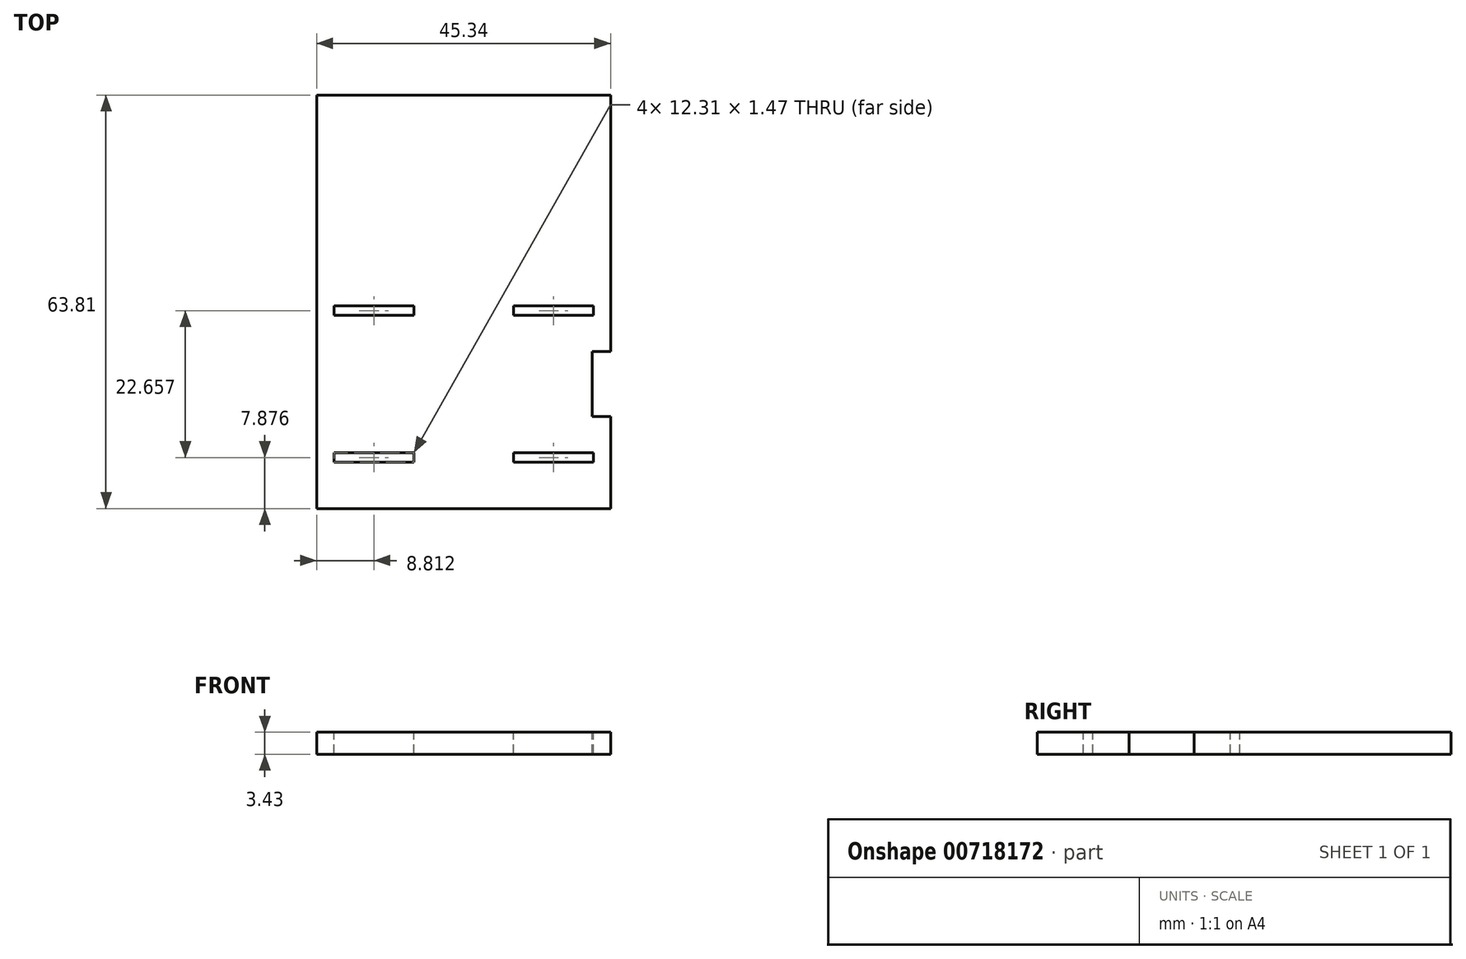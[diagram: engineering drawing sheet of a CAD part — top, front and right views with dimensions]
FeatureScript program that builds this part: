
annotation { "Feature Type Name" : "Feature", "Feature Type Description" : "" }
export const myFeature = defineFeature(function(context is Context, id is Id, definition is map)
    precondition{}
    {
        {
            var Q0;
            Q0=qCreatedBy(makeId("Top.planeOp"),FACE);
            var sketch = newSketch(context, id + "F0", { "sketchPlane" : qUnion([Q0])});
            skLineSegment(sketch, "E0.bottom", {"start": v(-23.55, 31.02) * mm, "end": v(21.8, 31.02) * mm});
            skLineSegment(sketch, "E0.top", {"start": v(-23.55, -7.39) * mm, "end": v(21.8, -7.39) * mm});
            skLineSegment(sketch, "E0.left", {"start": v(-23.55, 31.02) * mm, "end": v(-23.55, -7.39) * mm});
            skLineSegment(sketch, "E0.right", {"start": v(21.8, 31.02) * mm, "end": v(21.8, -7.39) * mm});
            skSolve(sketch);
        }
        {
            var Q0;
            Q0=makeQuery(id+"F0.imprint","IMPRINT",FACE,{"disambiguationData":[TD([[makeQuery(id+"F0.imprint","IMPRINT",EDGE,{"derivedFrom":sQuery(id+"F0.wireOp",EDGE,"E0.bottom")}),-1.0]])]});
            extrude(context, id + "F1", {"entities" : qUnion([Q0]), "depth" : 3.43 * mm, "offsetDistance" : 25.4 * mm});
        }
        {
            var Q0;
            Q0=makeQuery(id+"F1.opExtrude","CAP_FACE",FACE,{"disambiguationData":[OSD([sQuery(id+"F0.wireOp",EDGE,"E0.bottom"),sQuery(id+"F0.wireOp",EDGE,"E0.top"),sQuery(id+"F0.wireOp",EDGE,"E0.left"),sQuery(id+"F0.wireOp",EDGE,"E0.right")])],"isStart":false});
            var sketch = newSketch(context, id + "F2", { "sketchPlane" : qUnion([Q0])});
            skLineSegment(sketch, "E1", {"start": v(21.8, 31.02) * mm, "end": v(21.8, 23.14) * mm});
            skLineSegment(sketch, "E2", {"start": v(21.8, -7.39) * mm, "end": v(21.8, 0.49) * mm});
            skLineSegment(sketch, "E3", {"start": v(-23.55, -7.39) * mm, "end": v(-23.55, 0.49) * mm});
            skLineSegment(sketch, "E4.left", {"start": v(21.8, 1.22) * mm, "end": v(21.8, -0.25) * mm});
            skLineSegment(sketch, "E4.right", {"start": v(-23.55, 1.22) * mm, "end": v(-23.55, -0.25) * mm});
            skLineSegment(sketch, "E5.left", {"start": v(-23.55, 22.4) * mm, "end": v(-23.55, 23.88) * mm});
            skLineSegment(sketch, "E5.right", {"start": v(21.8, 22.4) * mm, "end": v(21.8, 23.88) * mm});
            skLineSegment(sketch, "E6", {"start": v(-8.55, 23.88) * mm, "end": v(-20.9, 23.88) * mm});
            skLineSegment(sketch, "E7", {"start": v(-20.9, 22.4) * mm, "end": v(-8.58, 22.4) * mm});
            skLineSegment(sketch, "E8", {"start": v(-20.9, 23.88) * mm, "end": v(-8.55, 23.88) * mm});
            skLineSegment(sketch, "E9.bottom", {"start": v(-20.9, 23.88) * mm, "end": v(-8.58, 23.88) * mm});
            skLineSegment(sketch, "E9.left", {"start": v(-20.9, 23.88) * mm, "end": v(-20.9, 22.4) * mm});
            skLineSegment(sketch, "E9.right", {"start": v(-8.58, 23.88) * mm, "end": v(-8.58, 22.4) * mm});
            skLineSegment(sketch, "E10.MirrorCS", {"start": v(19.14, 23.88) * mm, "end": v(19.14, 22.4) * mm});
            skLineSegment(sketch, "E11.MirrorCS", {"start": v(19.14, 22.4) * mm, "end": v(6.83, 22.4) * mm});
            skLineSegment(sketch, "E12.MirrorCS", {"start": v(6.83, 23.88) * mm, "end": v(6.83, 22.4) * mm});
            skLineSegment(sketch, "E13.bottom", {"start": v(-20.9, -0.25) * mm, "end": v(-8.58, -0.25) * mm});
            skLineSegment(sketch, "E13.top", {"start": v(-20.9, 1.22) * mm, "end": v(-8.58, 1.22) * mm});
            skLineSegment(sketch, "E13.left", {"start": v(-20.9, -0.25) * mm, "end": v(-20.9, 1.22) * mm});
            skLineSegment(sketch, "E13.right", {"start": v(-8.58, -0.25) * mm, "end": v(-8.58, 1.22) * mm});
            skLineSegment(sketch, "E14", {"start": v(6.83, 23.88) * mm, "end": v(19.14, 23.88) * mm});
            skLineSegment(sketch, "E15.MirrorCS", {"start": v(6.83, -0.25) * mm, "end": v(6.83, 1.22) * mm});
            skLineSegment(sketch, "E16.MirrorCS", {"start": v(19.14, 1.22) * mm, "end": v(6.83, 1.22) * mm});
            skLineSegment(sketch, "E17.MirrorCS", {"start": v(19.14, -0.25) * mm, "end": v(6.83, -0.25) * mm});
            skLineSegment(sketch, "E18.MirrorCS", {"start": v(19.14, -0.25) * mm, "end": v(19.14, 1.22) * mm});
            skLineSegment(sketch, "E19.bottom", {"start": v(18.92, 6.8) * mm, "end": v(24.67, 6.8) * mm});
            skLineSegment(sketch, "E19.top", {"start": v(18.92, 16.82) * mm, "end": v(24.67, 16.82) * mm});
            skLineSegment(sketch, "E19.left", {"start": v(18.92, 6.8) * mm, "end": v(18.92, 16.82) * mm});
            skLineSegment(sketch, "E19.right", {"start": v(24.67, 6.8) * mm, "end": v(24.67, 16.82) * mm});
            skPoint(sketch, "E19.middle", {"position": v(21.8, 11.81) * mm});
            skSolve(sketch);
        }
        {
            var Q0;
            Q0 = qSketchRegion(id + "F2", true);
            extrude(context, id + "F3", {"entities" : qUnion([Q0]), "operationType" : NewBodyOperationType.REMOVE, "oppositeDirection" : true, "depth" : 25.4 * mm, "offsetDistance" : 25.4 * mm});
        }
        {
            var Q0;
            Q0=makeQuery(id+"F1.opExtrude","SWEPT_FACE",FACE,{"disambiguationData":[OSD([sQuery(id+"F0.wireOp",EDGE,"E0.bottom")])]});
            var sketch = newSketch(context, id + "F4", { "sketchPlane" : qUnion([Q0])});
            skSolve(sketch);
        }
        {
            var Q0;
            {var subQ0=sQuery(id+"F0.wireOp",EDGE,"E0.bottom");Q0=makeQuery(id+"F4.imprint","IMPRINT",FACE,{"disambiguationData":[TD([[makeQuery(id+"F4.imprint","IMPRINT",EDGE,{"derivedFrom":makeQuery(id+"F1.opExtrude","CAP_EDGE",EDGE,{"disambiguationData":[OSD([subQ0])],"isStart":true})}),-1.0]])]});}
            extrude(context, id + "F5", {"entities" : qUnion([Q0]), "operationType" : NewBodyOperationType.ADD, "depth" : 25.4 * mm, "offsetDistance" : 25.4 * mm});
        }
    });
